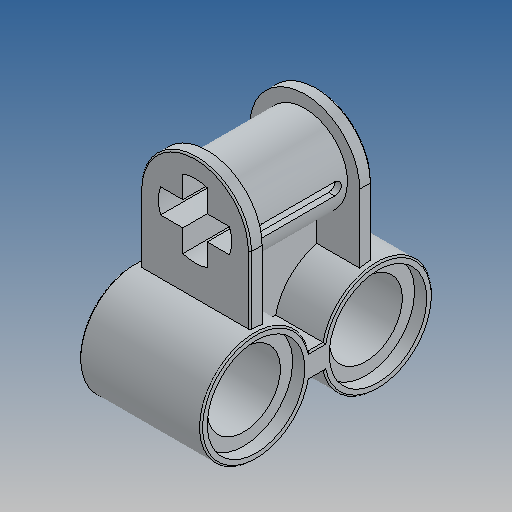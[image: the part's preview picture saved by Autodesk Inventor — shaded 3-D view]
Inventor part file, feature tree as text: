
AUTODESK INVENTOR PART (.ipt)
format: ipt  version: 2025 (Build 290162010, 162A)  size: 420,352 bytes
history: native  units: in
note: dims shown in document units (in); Inventor stores cm internally (conversion verified against a paired STEP export)
features: sketch x5, extrude x4, plane x1, revolve x1, mirror x1, fillet x1, other x1
ambient origin geometry x8: Origin, YZ Plane, XZ Plane, XY Plane, X Axis, Y Axis, Z Axis, Center Point
bodies: Solid1 (feature_tree)
feature tree (14):
  extrude  "Extrusion1"  Depth=0.063in
  plane  "Work Plane2"
  extrude  "Extrusion2"  Depth=0.315in TaperAngle=0.0deg
  extrude  "Extrusion3"  Depth=0.189in
  extrude  "Extrusion4"  Depth=0.0315in
  revolve  "Revolution1"  [1 undecoded]
  mirror  "Mirror1"
  fillet  "Fillet1"  Radius=0.063in
  sketch  "Sketch2"  dims[d0=0.2835in d1=0.063in]
  other  "Work Axis3"
  sketch  "Sketch3"  dims[d2=0.315in d3=0.315in d4=0.0in]
  sketch  "Sketch4"  dims[d6=90.0deg d7=0.189in]
  sketch  "Sketch5"  dims[d8=0.252in d9=0.0315in]
  sketch  "Sketch6"  dims[d10=90.0deg d12=0.2205in d14=0.063in d18=0.189in d20=0.063in d21=0.315in d22=0.0in d23=0.0315in d24=0.2205in d25=0.315in d26=0.0in d29=0.0315in d30=0.0in d39=0.0039in d40=0.315in d41=0.2835in d42=0.252in]
note: 1 required parameter value undecoded (feature->parameter linkage not recoverable at this tier; creation-order binding heuristic only, values carry confidence <= 0.55)
